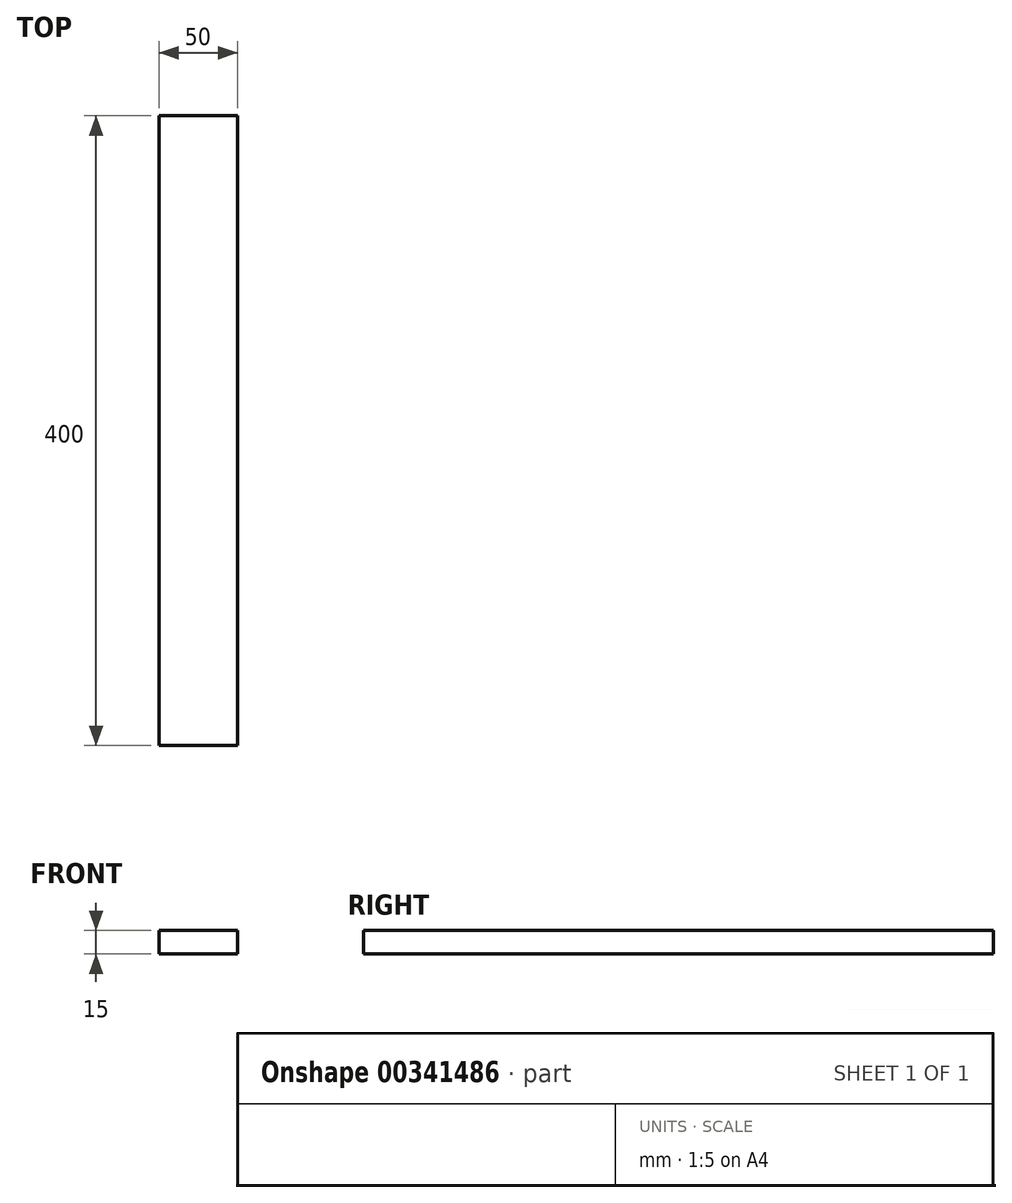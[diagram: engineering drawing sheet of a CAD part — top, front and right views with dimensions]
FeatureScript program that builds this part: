
annotation { "Feature Type Name" : "Feature", "Feature Type Description" : "" }
export const myFeature = defineFeature(function(context is Context, id is Id, definition is map)
    precondition{}
    {
        {
            var Q0;
            Q0=qCreatedBy(makeId("Top.planeOp"),FACE);
            var sketch = newSketch(context, id + "F0", { "sketchPlane" : qUnion([Q0])});
            skLineSegment(sketch, "E0.bottom", {"start": v(0, 0) * mm, "end": v(-50, 0) * mm});
            skLineSegment(sketch, "E0.top", {"start": v(0, 400) * mm, "end": v(-50, 400) * mm});
            skLineSegment(sketch, "E0.left", {"start": v(0, 0) * mm, "end": v(0, 400) * mm});
            skLineSegment(sketch, "E0.right", {"start": v(-50, 0) * mm, "end": v(-50, 400) * mm});
            skSolve(sketch);
        }
        {
            var Q0;
            Q0 = qSketchRegion(id + "F0", true);
            extrude(context, id + "F1", {"entities" : qUnion([Q0]), "depth" : 15 * mm});
        }
    });
